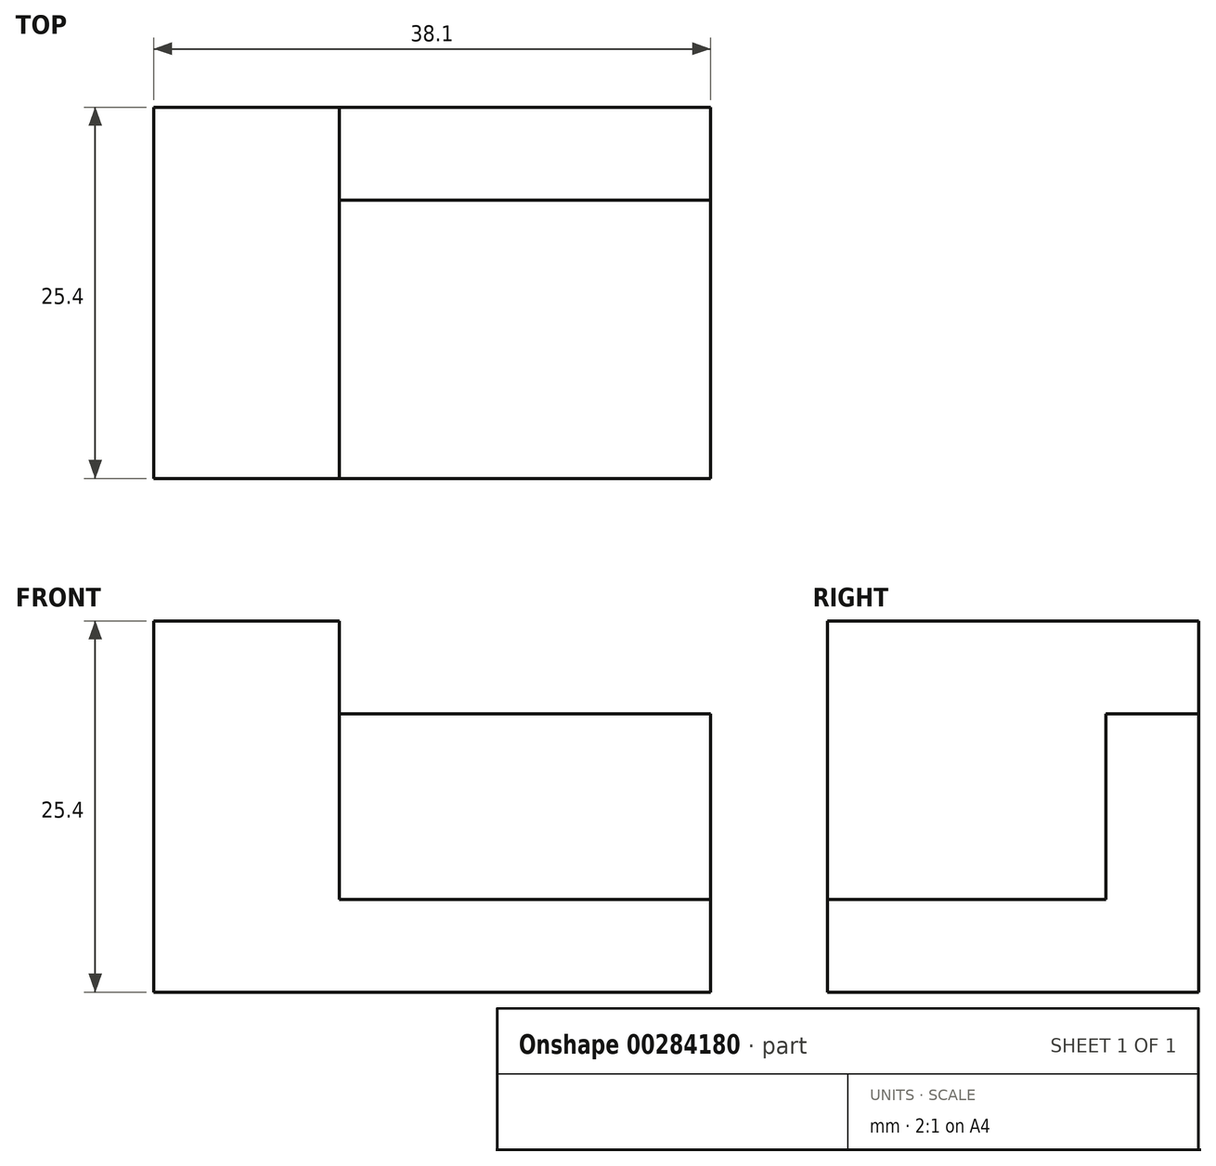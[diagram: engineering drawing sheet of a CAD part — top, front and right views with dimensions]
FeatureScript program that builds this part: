
annotation { "Feature Type Name" : "Feature", "Feature Type Description" : "" }
export const myFeature = defineFeature(function(context is Context, id is Id, definition is map)
    precondition{}
    {
        {
            var Q0;
            Q0=qCreatedBy(makeId("Front.planeOp"),FACE);
            var sketch = newSketch(context, id + "F0", { "sketchPlane" : qUnion([Q0])});
            skLineSegment(sketch, "E0", {"start": v(0, 0) * mm, "end": v(38.1, 0) * mm});
            skLineSegment(sketch, "E1", {"start": v(38.1, 0) * mm, "end": v(38.1, 19.05) * mm});
            skLineSegment(sketch, "E2", {"start": v(38.1, 19.05) * mm, "end": v(12.7, 19.05) * mm});
            skLineSegment(sketch, "E3", {"start": v(12.7, 19.05) * mm, "end": v(12.7, 25.4) * mm});
            skLineSegment(sketch, "E4", {"start": v(12.7, 25.4) * mm, "end": v(0, 25.4) * mm});
            skLineSegment(sketch, "E5", {"start": v(0, 25.4) * mm, "end": v(0, 0) * mm});
            skLineSegment(sketch, "E6", {"start": v(12.7, 19.05) * mm, "end": v(12.7, 6.35) * mm});
            skLineSegment(sketch, "E7", {"start": v(12.7, 6.35) * mm, "end": v(38.1, 6.35) * mm});
            skSolve(sketch);
        }
        {
            var Q0;
            Q0 = qSketchRegion(id + "F0", true);
            extrude(context, id + "F1", {"entities" : qUnion([Q0]), "depth" : 25.4 * mm, "symmetric" : true});
        }
        {
            var Q0;
            Q0=makeQuery(id+"F1.opExtrude","SWEPT_FACE",FACE,{"disambiguationData":[OSD([sQuery(id+"F0.wireOp",EDGE,"E1")])]});
            var sketch = newSketch(context, id + "F2", { "sketchPlane" : qUnion([Q0])});
            skLineSegment(sketch, "E8", {"start": v(-12.7, 0) * mm, "end": v(-12.7, 6.35) * mm});
            skLineSegment(sketch, "E9", {"start": v(-12.7, 6.35) * mm, "end": v(6.35, 6.35) * mm});
            skLineSegment(sketch, "E10", {"start": v(6.35, 6.35) * mm, "end": v(6.35, 19.05) * mm});
            skLineSegment(sketch, "E11", {"start": v(6.35, 19.05) * mm, "end": v(12.7, 19.05) * mm});
            skLineSegment(sketch, "E12", {"start": v(12.7, 19.05) * mm, "end": v(12.7, 0) * mm});
            skLineSegment(sketch, "E13", {"start": v(12.7, 0) * mm, "end": v(-12.7, 0) * mm});
            skSolve(sketch);
        }
        {
            var Q0;
            {var subQ0=sQuery(id+"F2.wireOp",EDGE,"E9");Q0=makeQuery(id+"F2.imprint","IMPRINT",FACE,{"disambiguationData":[TD([[makeQuery(id+"F2.imprint","IMPRINT",EDGE,{"derivedFrom":subQ0}),1.0]])]});}
            extrude(context, id + "F3", {"entities" : qUnion([Q0]), "operationType" : NewBodyOperationType.REMOVE, "oppositeDirection" : true, "depth" : 25.4 * mm});
        }
    });
